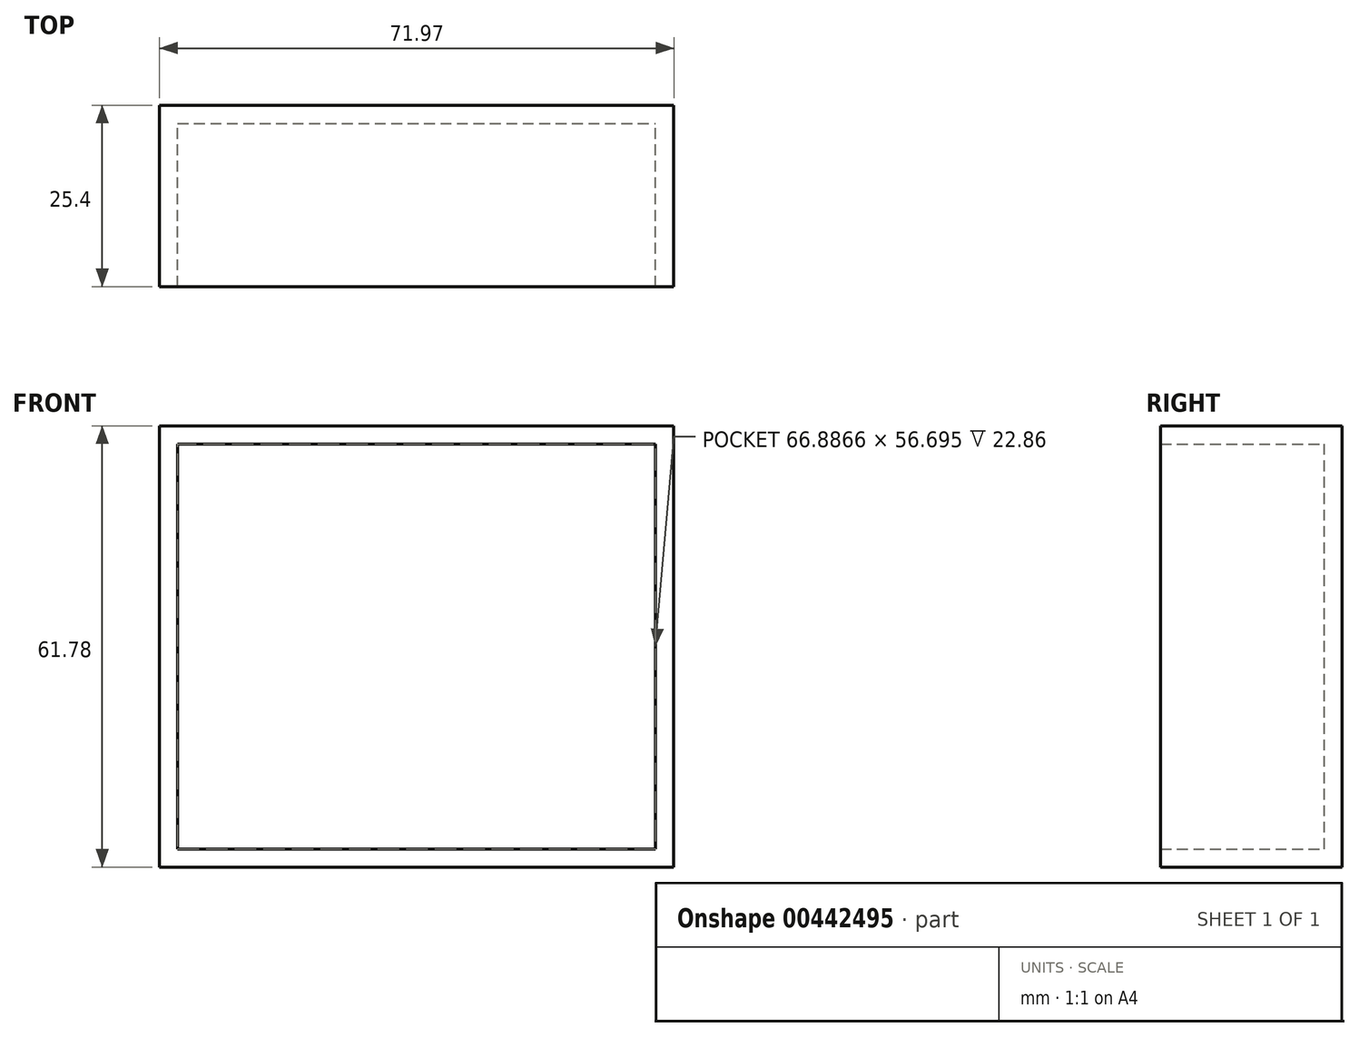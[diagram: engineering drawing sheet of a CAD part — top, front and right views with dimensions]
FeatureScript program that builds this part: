
annotation { "Feature Type Name" : "Feature", "Feature Type Description" : "" }
export const myFeature = defineFeature(function(context is Context, id is Id, definition is map)
    precondition{}
    {
        {
            var Q0;
            Q0=qCreatedBy(makeId("Front.planeOp"),FACE);
            var sketch = newSketch(context, id + "F0", { "sketchPlane" : qUnion([Q0])});
            skLineSegment(sketch, "E0.bottom", {"start": v(-40.85, 37.74) * mm, "end": v(31.12, 37.74) * mm});
            skLineSegment(sketch, "E0.top", {"start": v(-40.85, -24.04) * mm, "end": v(31.12, -24.04) * mm});
            skLineSegment(sketch, "E0.left", {"start": v(-40.85, 37.74) * mm, "end": v(-40.85, -24.04) * mm});
            skLineSegment(sketch, "E0.right", {"start": v(31.12, 37.74) * mm, "end": v(31.12, -24.04) * mm});
            skSolve(sketch);
        }
        {
            var Q0;
            Q0 = qSketchRegion(id + "F0", true);
            extrude(context, id + "F1", {"entities" : qUnion([Q0]), "depth" : 25.4 * mm});
        }
        {
            var Q0;
            Q0=makeQuery(id+"F1.opExtrude","CAP_FACE",FACE,{"disambiguationData":[OSD([sQuery(id+"F0.wireOp",EDGE,"E0.bottom"),sQuery(id+"F0.wireOp",EDGE,"E0.top"),sQuery(id+"F0.wireOp",EDGE,"E0.left"),sQuery(id+"F0.wireOp",EDGE,"E0.right")])],"isStart":false});
            var Q1;
            Q1=makeQuery(id+"F1.opExtrude","SWEPT_BODY",BODY,{"disambiguationData":[OSD([sQuery(id+"F0.wireOp",EDGE,"E0.bottom"),sQuery(id+"F0.wireOp",EDGE,"E0.top"),sQuery(id+"F0.wireOp",EDGE,"E0.left"),sQuery(id+"F0.wireOp",EDGE,"E0.right")])]});
            shell(context, id + "F2", {"entities" : qUnion([Q0]), "parts" : qUnion([Q1]), "thickness" : 2.54 * mm});
        }
    });
